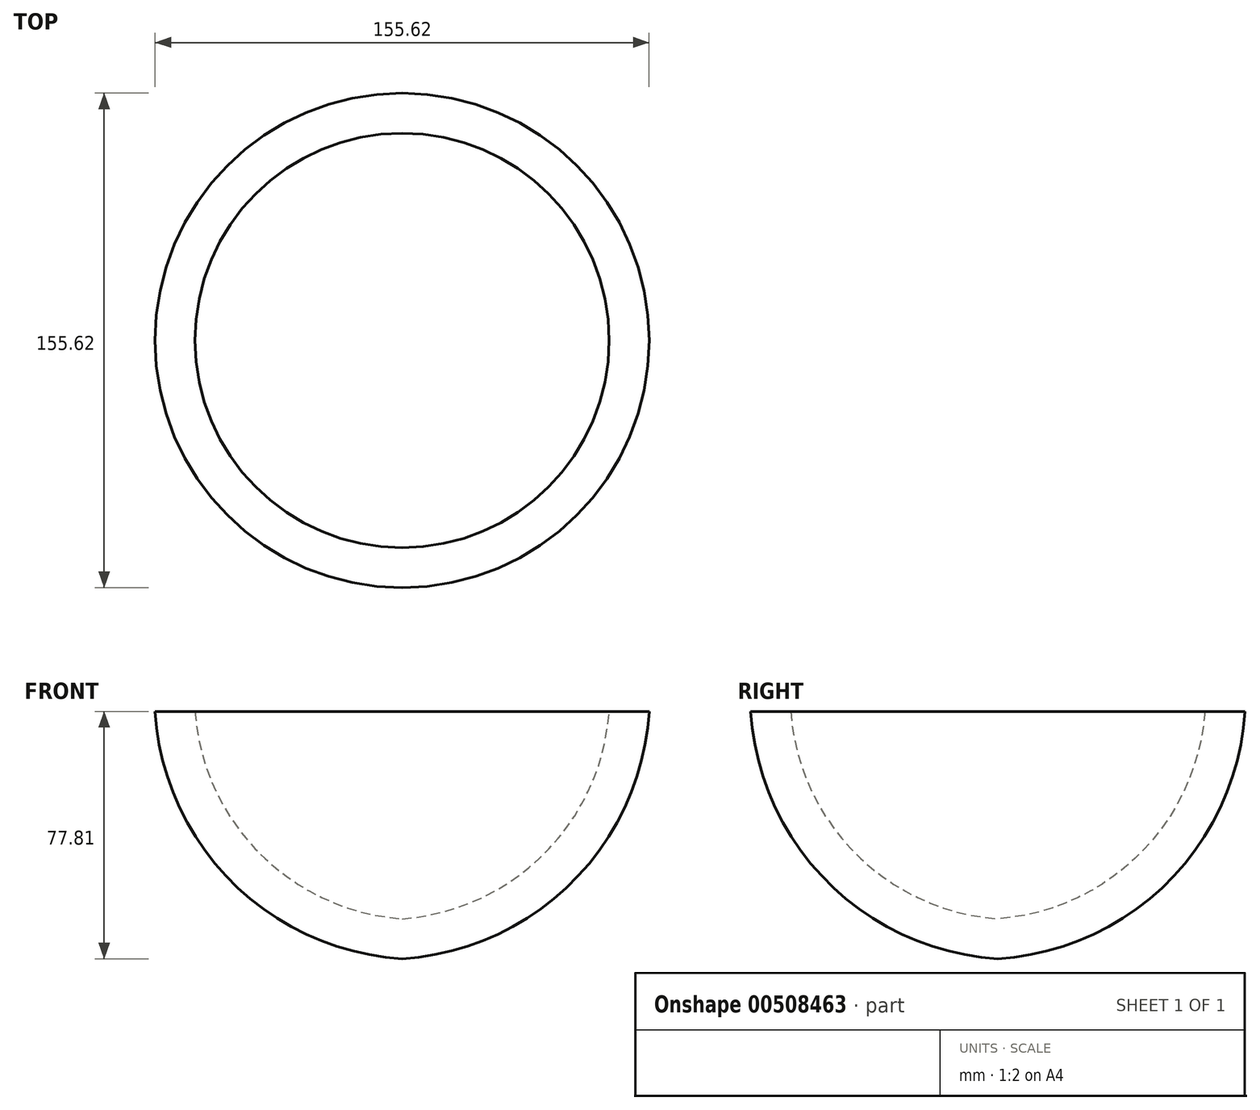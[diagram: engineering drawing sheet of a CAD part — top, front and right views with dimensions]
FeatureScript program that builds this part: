
annotation { "Feature Type Name" : "Feature", "Feature Type Description" : "" }
export const myFeature = defineFeature(function(context is Context, id is Id, definition is map)
    precondition{}
    {
        {
            var Q0;
            Q0=qCreatedBy(makeId("Front.planeOp"),FACE);
            var sketch = newSketch(context, id + "F0", { "sketchPlane" : qUnion([Q0])});
            skArc(sketch, "E0", {"start": v(0, -65.23) * mm, "mid": v(44.76, -44.76) * mm, "end": v(65.23, 0) * mm});
            skLineSegment(sketch, "E1", {"start": v(65.23, 0) * mm, "end": v(77.81, 0) * mm});
            skLineSegment(sketch, "E2", {"start": v(-41.1, -65.42) * mm, "end": v(45.05, -65.42) * mm, "construction": true});
            skArc(sketch, "E3", {"start": v(0, -77.81) * mm, "mid": v(53.63, -53.63) * mm, "end": v(77.81, 0) * mm});
            skLineSegment(sketch, "E4", {"start": v(0, -77.81) * mm, "end": v(0, -65.23) * mm});
            skSolve(sketch);
        }
        {
            var Q0;
            Q0 = qSketchRegion(id + "F0", true);
            var Q1;
            Q1=sQuery(id+"F0.wireOp",EDGE,"E4");
            revolve(context, id + "F1", {"entities" : qUnion([Q0]), "axis" : qUnion([Q1]), "revolveType" : RevolveType.FULL});
        }
    });
